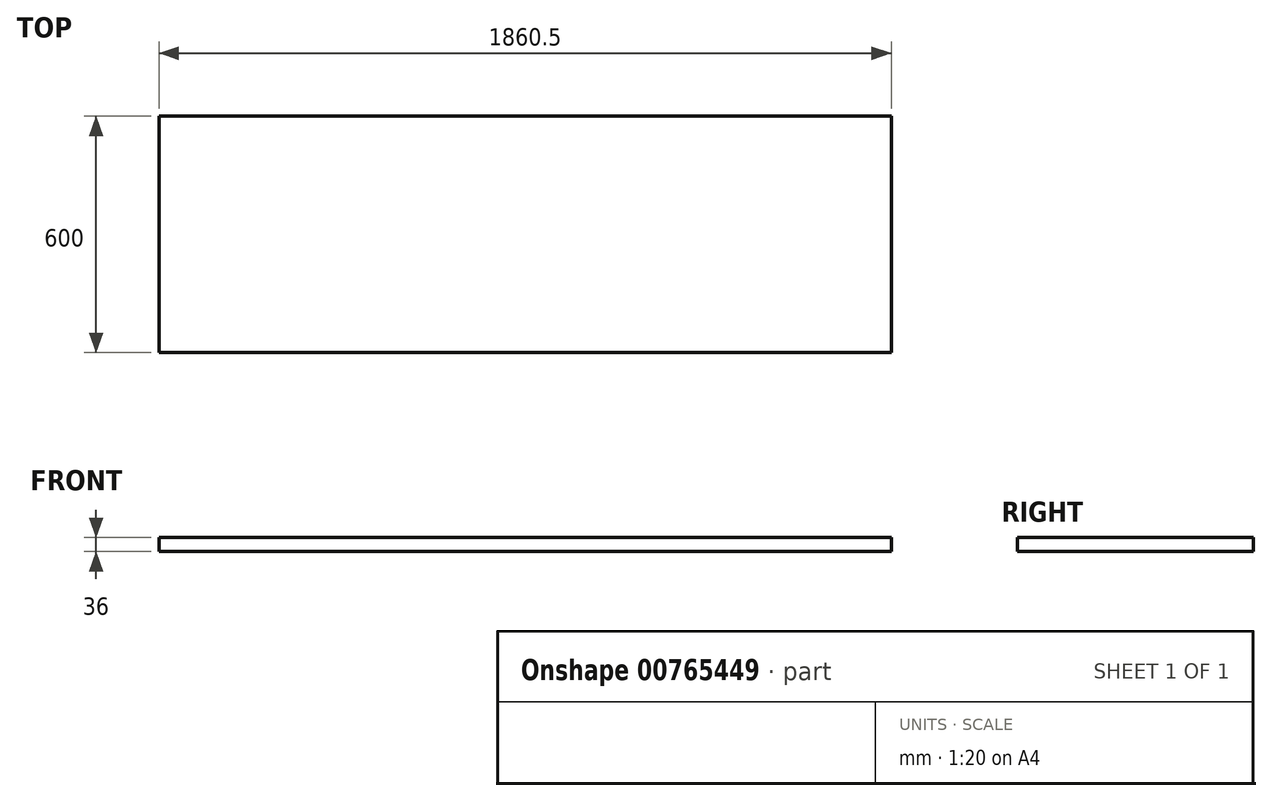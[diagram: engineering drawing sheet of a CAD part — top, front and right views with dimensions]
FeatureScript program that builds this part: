
annotation { "Feature Type Name" : "Feature", "Feature Type Description" : "" }
export const myFeature = defineFeature(function(context is Context, id is Id, definition is map)
    precondition{}
    {
        {
            var Q0;
            Q0=qCreatedBy(makeId("Top.planeOp"),FACE);
            var sketch = newSketch(context, id + "F0", { "sketchPlane" : qUnion([Q0])});
            skLineSegment(sketch, "E0.bottom", {"start": v(-930.25, -300) * mm, "end": v(930.25, -300) * mm});
            skLineSegment(sketch, "E0.top", {"start": v(-930.25, 300) * mm, "end": v(930.25, 300) * mm});
            skLineSegment(sketch, "E0.left", {"start": v(-930.25, -300) * mm, "end": v(-930.25, 300) * mm});
            skLineSegment(sketch, "E0.right", {"start": v(930.25, -300) * mm, "end": v(930.25, 300) * mm});
            skPoint(sketch, "E0.middle", {"position": v(0, 0) * mm});
            skSolve(sketch);
        }
        {
            var Q0;
            Q0 = qSketchRegion(id + "F0", true);
            extrude(context, id + "F1", {"entities" : qUnion([Q0]), "depth" : 36 * mm, "offsetDistance" : 25 * mm});
        }
    });
